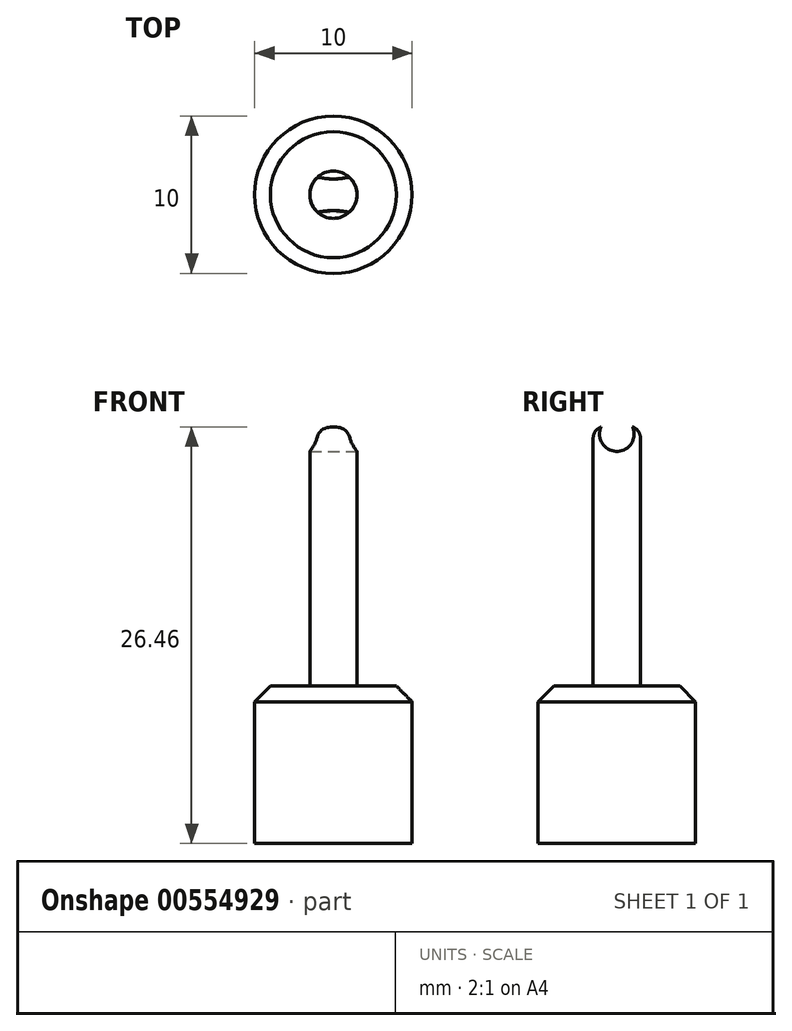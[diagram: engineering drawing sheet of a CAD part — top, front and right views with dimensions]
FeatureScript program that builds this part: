
annotation { "Feature Type Name" : "Feature", "Feature Type Description" : "" }
export const myFeature = defineFeature(function(context is Context, id is Id, definition is map)
    precondition{}
    {
        {
            var Q0;
            Q0=qCreatedBy(makeId("Top.planeOp"),FACE);
            var sketch = newSketch(context, id + "F0", { "sketchPlane" : qUnion([Q0])});
            skCircle(sketch, "E0", {"center": v(0, 0) * mm, "radius": 5 * mm});
            skSolve(sketch);
        }
        {
            var Q0;
            Q0 = qSketchRegion(id + "F0", true);
            extrude(context, id + "F1", {"entities" : qUnion([Q0]), "depth" : 10 * mm, "offsetDistance" : 25 * mm});
        }
        {
            var Q0;
            Q0=makeQuery(id+"F1.opExtrude","CAP_FACE",FACE,{"disambiguationData":[OSD([sQuery(id+"F0.wireOp",EDGE,"E0")])],"isStart":false});
            var sketch = newSketch(context, id + "F2", { "sketchPlane" : qUnion([Q0])});
            skCircle(sketch, "E1", {"center": v(0, 0) * mm, "radius": 1.5 * mm});
            skSolve(sketch);
        }
        {
            var Q0;
            Q0=makeQuery(id+"F2.imprint","IMPRINT",FACE,{"disambiguationData":[TD([[makeQuery(id+"F2.imprint","IMPRINT",EDGE,{"derivedFrom":sQuery(id+"F2.wireOp",EDGE,"E1")}),1.0]])]});
            extrude(context, id + "F3", {"entities" : qUnion([Q0]), "operationType" : NewBodyOperationType.ADD, "depth" : 16 * mm, "offsetDistance" : 25 * mm});
        }
        {
            var Q0;
            Q0=qCreatedBy(makeId("Right.planeOp"),FACE);
            var sketch = newSketch(context, id + "F4", { "sketchPlane" : qUnion([Q0])});
            skLineSegment(sketch, "E2.0", {"start": v(-1.5, 26) * mm, "end": v(1.5, 26) * mm});
            skCircle(sketch, "E3", {"center": v(0, 26) * mm, "radius": 1.5 * mm});
            skSolve(sketch);
        }
        {
            var Q0;
            {var subQ0=sQuery(id+"F4.wireOp",EDGE,"E2.0");Q0=makeQuery(id+"F4.imprint","IMPRINT",FACE,{"disambiguationData":[TD([[makeQuery(id+"F4.imprint","IMPRINT",EDGE,{"derivedFrom":subQ0}),1.0]])]});}
            var Q1;
            Q1=sQuery(id+"F4.wireOp",EDGE,"E2.0");
            revolve(context, id + "F5", {"operationType" : NewBodyOperationType.ADD, "entities" : qUnion([Q0]), "axis" : qUnion([Q1]), "revolveType" : RevolveType.FULL});
        }
        {
            var Q0;
            Q0=qCreatedBy(makeId("Right.planeOp"),FACE);
            var sketch = newSketch(context, id + "F6", { "sketchPlane" : qUnion([Q0])});
            skLineSegment(sketch, "E4", {"start": v(-0.98, 26.5) * mm, "end": v(-1.41, 26.5) * mm});
            skArc(sketch, "E5", {"start": v(-0.98, 26.5) * mm, "mid": v(0, 24.9) * mm, "end": v(0.98, 26.5) * mm});
            skPoint(sketch, "E6.orphan", {"position": v(1.5, 26) * mm});
            skPoint(sketch, "E7.orphan", {"position": v(-1.5, 26) * mm});
            skArc(sketch, "E8", {"start": v(1.41, 26.5) * mm, "mid": v(0, 27.5) * mm, "end": v(-1.41, 26.5) * mm});
            skLineSegment(sketch, "E9", {"start": v(1.41, 26.5) * mm, "end": v(0.98, 26.5) * mm});
            skSolve(sketch);
        }
        {
            var Q0;
            Q0=makeQuery(id+"F1.opExtrude","CAP_EDGE",EDGE,{"disambiguationData":[OSD([sQuery(id+"F0.wireOp",EDGE,"E0")])],"isStart":false});
            var Q1;
            Q1=makeQuery(id+"F3.opExtrude","CAP_EDGE",EDGE,{"disambiguationData":[OSD([sQuery(id+"F2.wireOp",EDGE,"E1")])],"isStart":true});
            chamfer(context, id + "F7", {"entities" : qUnion([Q0, Q1]), "width" : 1 * mm, "tangentPropagation" : true});
        }
        {
            var Q0;
            Q0 = qSketchRegion(id + "F6", true);
            extrude(context, id + "F8", {"entities" : qUnion([Q0]), "operationType" : NewBodyOperationType.REMOVE, "endBound" : BoundingType.SYMMETRIC, "oppositeDirection" : true, "depth" : 25 * mm, "offsetDistance" : 25 * mm});
        }
        {
            var Q0;
            Q0=makeQuery(id+"F8.boolean.opBoolean","INTERSECT",EDGE,{"derivedFrom":[makeQuery(id+"F5.opRevolve","SWEPT_FACE",FACE,{"disambiguationData":[OSD([sQuery(id+"F4.wireOp",EDGE,"E3")])]}),makeQuery(id+"F8.opExtrude","SWEPT_FACE",FACE,{"disambiguationData":[OSD([sQuery(id+"F6.wireOp",EDGE,"E9")])]})]});
            var Q1;
            Q1=makeQuery(id+"F8.boolean.opBoolean","INTERSECT",EDGE,{"derivedFrom":[makeQuery(id+"F5.opRevolve","SWEPT_FACE",FACE,{"disambiguationData":[OSD([sQuery(id+"F4.wireOp",EDGE,"E3")])]}),makeQuery(id+"F8.opExtrude","SWEPT_FACE",FACE,{"disambiguationData":[OSD([sQuery(id+"F6.wireOp",EDGE,"E4")])]})]});
            fillet(context, id + "F9", {"entities" : qUnion([Q0, Q1]), "radius" : .75 * mm, "tangentPropagation" : true, "allowEdgeOverflow" : false});
        }
    });
